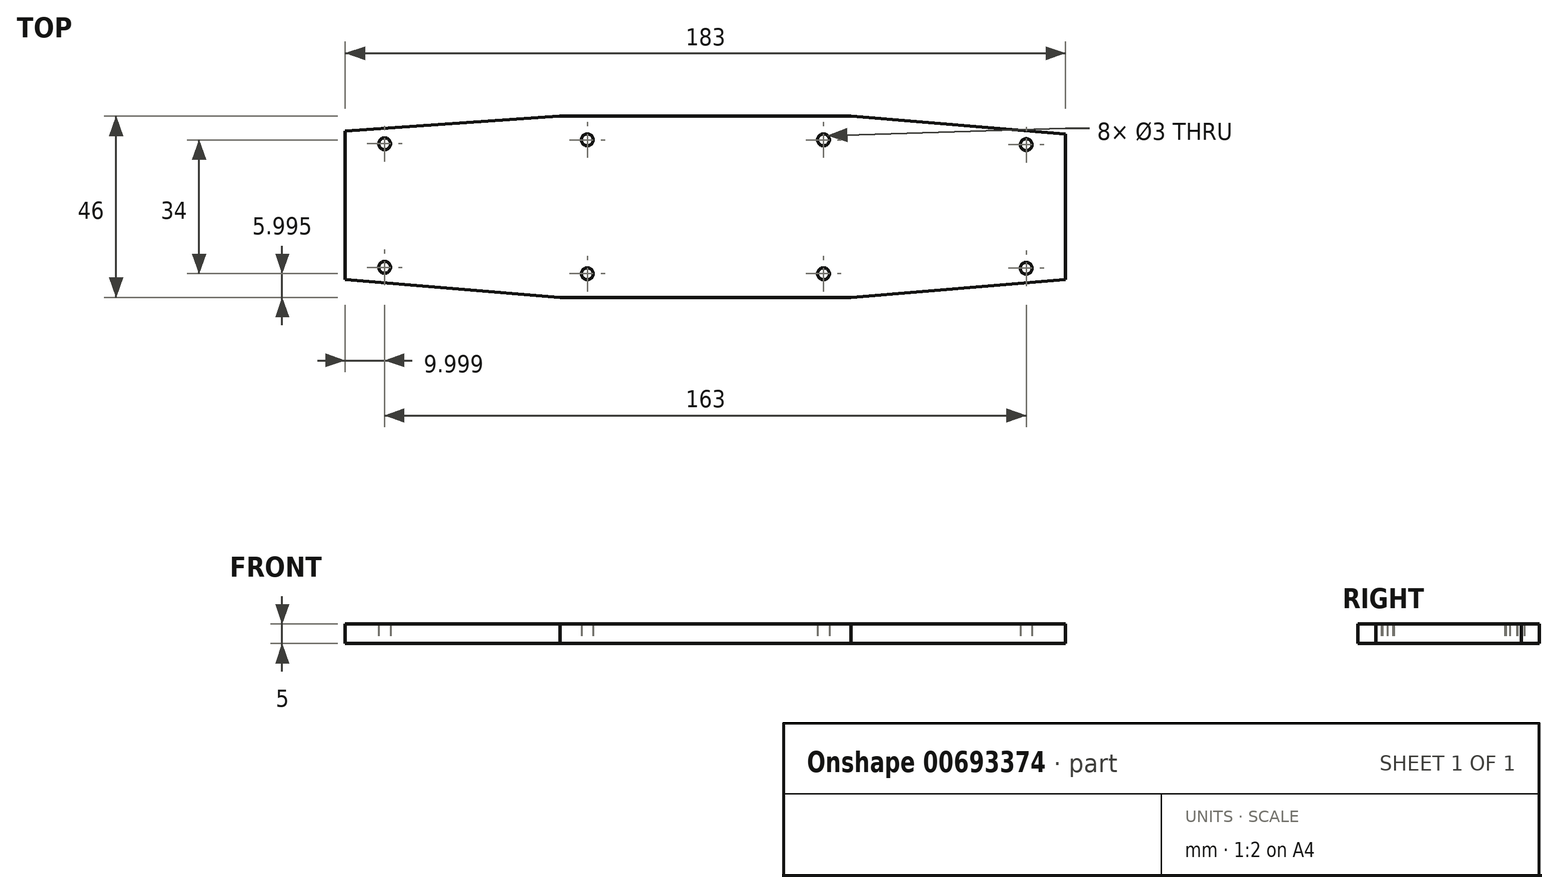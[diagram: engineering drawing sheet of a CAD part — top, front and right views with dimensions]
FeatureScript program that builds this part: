
annotation { "Feature Type Name" : "Feature", "Feature Type Description" : "" }
export const myFeature = defineFeature(function(context is Context, id is Id, definition is map)
    precondition{}
    {
        {
            var Q0;
            Q0=qCreatedBy(makeId("Top.planeOp"),FACE);
            var sketch = newSketch(context, id + "F0", { "sketchPlane" : qUnion([Q0])});
            skLineSegment(sketch, "E0.top", {"start": v(-31.6, -24.44) * mm, "end": v(42.4, -24.44) * mm});
            skCircle(sketch, "E1", {"center": v(86.89, 14.34) * mm, "radius": 1.5 * mm});
            skCircle(sketch, "E2", {"center": v(86.89, -17.06) * mm, "radius": 1.5 * mm});
            skCircle(sketch, "E3", {"center": v(35.39, 15.56) * mm, "radius": 1.5 * mm});
            skCircle(sketch, "E4", {"center": v(35.39, -18.44) * mm, "radius": 1.5 * mm});
            skCircle(sketch, "E5", {"center": v(-24.61, 15.56) * mm, "radius": 1.5 * mm});
            skCircle(sketch, "E6", {"center": v(-24.61, -18.44) * mm, "radius": 1.5 * mm});
            skCircle(sketch, "E7", {"center": v(-76.11, 14.57) * mm, "radius": 1.5 * mm});
            skCircle(sketch, "E8", {"center": v(-76.11, -16.83) * mm, "radius": 1.5 * mm});
            skLineSegment(sketch, "E9", {"start": v(-31.62, 21.56) * mm, "end": v(-86.2, 17.78) * mm});
            skLineSegment(sketch, "E10", {"start": v(42.4, -24.44) * mm, "end": v(96.91, -19.91) * mm});
            skLineSegment(sketch, "E11", {"start": v(42.38, 21.56) * mm, "end": v(96.89, 17.03) * mm});
            skLineSegment(sketch, "E12", {"start": v(-31.6, -24.44) * mm, "end": v(-86.11, -19.91) * mm});
            skLineSegment(sketch, "E13", {"start": v(-86.11, 17.78) * mm, "end": v(-86.11, -19.91) * mm});
            skLineSegment(sketch, "E14", {"start": v(-31.62, 21.56) * mm, "end": v(42.38, 21.56) * mm});
            skPoint(sketch, "E0.left.start.orphan", {"position": v(-86.2, 21.56) * mm});
            skLineSegment(sketch, "E15", {"start": v(96.89, 17.03) * mm, "end": v(96.89, -19.92) * mm});
            skSolve(sketch);
        }
        {
            var Q0;
            {var subQ3=sQuery(id+"F0.wireOp",EDGE,"E0.top");Q0=makeQuery(id+"F0.imprint","IMPRINT",FACE,{"disambiguationData":[TD([[makeQuery(id+"F0.imprint","IMPRINT",EDGE,{"derivedFrom":subQ3}),1.0]])]});}
            extrude(context, id + "F1", {"entities" : qUnion([Q0]), "depth" : 5 * mm, "offsetDistance" : 25 * mm});
        }
    });
